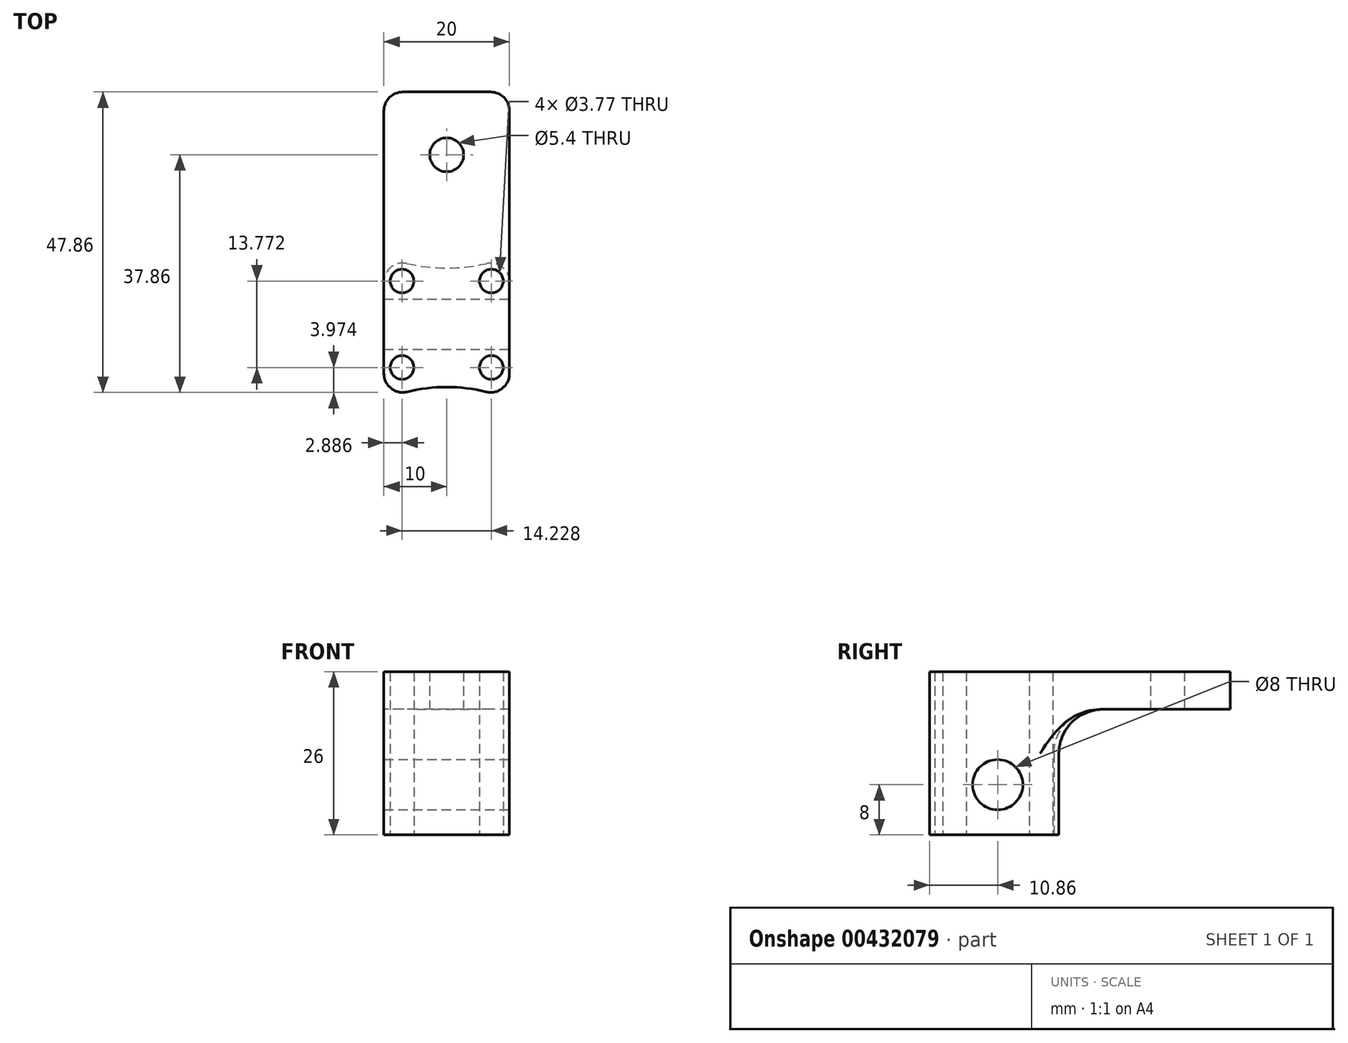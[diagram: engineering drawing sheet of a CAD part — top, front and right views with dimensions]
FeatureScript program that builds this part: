
annotation { "Feature Type Name" : "Feature", "Feature Type Description" : "" }
export const myFeature = defineFeature(function(context is Context, id is Id, definition is map)
    precondition{}
    {
        {
            var Q0;
            Q0=qCreatedBy(makeId("Top.planeOp"),FACE);
            var sketch = newSketch(context, id + "F0", { "sketchPlane" : qUnion([Q0])});
            skLineSegment(sketch, "E0.bottom", {"start": v(10, -24.5) * mm, "end": v(-10, -24.5) * mm});
            skLineSegment(sketch, "E0.top", {"start": v(10, 24.5) * mm, "end": v(-10, 24.5) * mm});
            skLineSegment(sketch, "E0.left", {"start": v(10, -24.5) * mm, "end": v(10, 24.5) * mm});
            skLineSegment(sketch, "E0.right", {"start": v(-10, -24.5) * mm, "end": v(-10, 24.5) * mm});
            skPoint(sketch, "E0.middle", {"position": v(0, 0) * mm});
            skLineSegment(sketch, "E1", {"start": v(-10, 4.5) * mm, "end": v(10, 4.5) * mm, "construction": true});
            skLineSegment(sketch, "E2", {"start": v(-10, -12.5) * mm, "end": v(10, -12.5) * mm, "construction": true});
            skCircle(sketch, "E3", {"center": v(-7.11, -5.61) * mm, "radius": 1.89 * mm});
            skLineSegment(sketch, "E4", {"start": v(-10, -8.5) * mm, "end": v(10, -8.5) * mm, "construction": true});
            skLineSegment(sketch, "E5", {"start": v(-10, -16.5) * mm, "end": v(10, -16.5) * mm, "construction": true});
            skCircle(sketch, "E6.MirrorC", {"center": v(7.11, -5.61) * mm, "radius": 1.89 * mm});
            skCircle(sketch, "E7.MirrorC", {"center": v(7.11, -19.39) * mm, "radius": 1.89 * mm});
            skCircle(sketch, "E8.MirrorC", {"center": v(-7.11, -19.39) * mm, "radius": 1.89 * mm});
            skCircle(sketch, "E9", {"center": v(0, 14.5) * mm, "radius": 2.7 * mm});
            skPoint(sketch, "E9.centerSnap0", {"position": v(0, 24.5) * mm});
            skLineSegment(sketch, "E10", {"start": v(10, -0.5) * mm, "end": v(-10, -0.5) * mm, "construction": true});
            skLineSegment(sketch, "E11", {"start": v(-10, -1.73) * mm, "end": v(10, -1.73) * mm});
            skSolve(sketch);
        }
        {
            var Q0;
            Q0=makeQuery(id+"F0.imprint","IMPRINT",FACE,{"disambiguationData":[TD([[makeQuery(id+"F0.imprint","IMPRINT",EDGE,{"derivedFrom":sQuery(id+"F0.wireOp",EDGE,"E0.bottom")}),-1.0]])]});
            var Q1;
            {var subQ1=sQuery(id+"F0.wireOp",EDGE,"E0.top");Q1=makeQuery(id+"F0.imprint","IMPRINT",FACE,{"disambiguationData":[TD([[makeQuery(id+"F0.imprint","IMPRINT",EDGE,{"derivedFrom":subQ1}),1.0]])]});}
            extrude(context, id + "F1", {"entities" : qUnion([Q0, Q1]), "depth" : 6 * mm});
        }
        {
            var Q0;
            {var subQ1=sQuery(id+"F0.wireOp",EDGE,"E0.bottom");Q0=makeQuery(id+"F0.imprint","IMPRINT",FACE,{"disambiguationData":[TD([[makeQuery(id+"F0.imprint","IMPRINT",EDGE,{"derivedFrom":subQ1}),-1.0]])]});}
            extrude(context, id + "F2", {"entities" : qUnion([Q0]), "operationType" : NewBodyOperationType.ADD, "oppositeDirection" : true, "depth" : 20 * mm});
        }
        {
            var Q0;
            {var subQ0=sQuery(id+"F0.wireOp",EDGE,"E0.left");Q0=makeQuery(id+"F2.boolean.opBoolean","MERGE",FACE,{"derivedFrom":[makeQuery(id+"F1.opExtrude","SWEPT_FACE",FACE,{"disambiguationData":[OSD([subQ0])]}),makeQuery(id+"F2.opExtrude","SWEPT_FACE",FACE,{"disambiguationData":[OSD([subQ0])]})]});}
            var sketch = newSketch(context, id + "F3", { "sketchPlane" : qUnion([Q0])});
            skCircle(sketch, "E12", {"center": v(-12.5, -12) * mm, "radius": 4 * mm});
            skLineSegment(sketch, "E13", {"start": v(-1.73, -12) * mm, "end": v(-24.5, -12) * mm, "construction": true});
            skSolve(sketch);
        }
        {
            var Q0;
            Q0=makeQuery(id+"F3.imprint","IMPRINT",FACE,{"disambiguationData":[TD([[makeQuery(id+"F3.imprint","IMPRINT",EDGE,{"derivedFrom":sQuery(id+"F3.wireOp",EDGE,"E12")}),1.0]])]});
            extrude(context, id + "F4", {"entities" : qUnion([Q0]), "operationType" : NewBodyOperationType.REMOVE, "oppositeDirection" : true, "depth" : 25 * mm});
        }
        {
            var Q0;
            Q0=makeQuery(id+"F2.opExtrude","CAP_FACE",FACE,{"disambiguationData":[OSD([sQuery(id+"F0.wireOp",EDGE,"E0.bottom"),sQuery(id+"F0.wireOp",EDGE,"E0.left"),sQuery(id+"F0.wireOp",EDGE,"E0.right"),sQuery(id+"F0.wireOp",EDGE,"E3"),sQuery(id+"F0.wireOp",EDGE,"E6.MirrorC"),sQuery(id+"F0.wireOp",EDGE,"E7.MirrorC"),sQuery(id+"F0.wireOp",EDGE,"E8.MirrorC"),sQuery(id+"F0.wireOp",EDGE,"E11")])],"isStart":false});
            var sketch = newSketch(context, id + "F5", { "sketchPlane" : qUnion([Q0])});
            skArc(sketch, "E14", {"start": v(10, 1.73) * mm, "mid": v(0, 3.55) * mm, "end": v(-10, 1.73) * mm});
            skArc(sketch, "E15", {"start": v(-10, 24.5) * mm, "mid": v(0, 22.5) * mm, "end": v(10, 24.5) * mm});
            skSolve(sketch);
        }
        {
            var Q0;
            Q0=makeQuery(id+"F5.imprint","IMPRINT",FACE,{"disambiguationData":[TD([[makeQuery(id+"F5.imprint","IMPRINT",EDGE,{"derivedFrom":sQuery(id+"F5.wireOp",EDGE,"E14")}),1.0]])]});
            var Q1;
            Q1=makeQuery(id+"F1.opExtrude","CAP_FACE",FACE,{"disambiguationData":[OSD([sQuery(id+"F0.wireOp",EDGE,"E0.bottom"),sQuery(id+"F0.wireOp",EDGE,"E0.top"),sQuery(id+"F0.wireOp",EDGE,"E0.left"),sQuery(id+"F0.wireOp",EDGE,"E0.right"),sQuery(id+"F0.wireOp",EDGE,"E3"),sQuery(id+"F0.wireOp",EDGE,"E6.MirrorC"),sQuery(id+"F0.wireOp",EDGE,"E7.MirrorC"),sQuery(id+"F0.wireOp",EDGE,"E8.MirrorC"),sQuery(id+"F0.wireOp",EDGE,"E9")])],"isStart":true});
            extrude(context, id + "F6", {"entities" : qUnion([Q0]), "operationType" : NewBodyOperationType.REMOVE, "endBound" : BoundingType.UP_TO_SURFACE, "oppositeDirection" : true, "endBoundEntityFace" : qUnion([Q1]), "depth" : 25 * mm});
        }
        {
            var Q0;
            Q0=makeQuery(id+"F5.imprint","IMPRINT",FACE,{"disambiguationData":[TD([[makeQuery(id+"F5.imprint","IMPRINT",EDGE,{"derivedFrom":sQuery(id+"F5.wireOp",EDGE,"E15")}),1.0]])]});
            extrude(context, id + "F7", {"entities" : qUnion([Q0]), "operationType" : NewBodyOperationType.REMOVE, "endBound" : BoundingType.THROUGH_ALL, "oppositeDirection" : true, "depth" : 25 * mm});
        }
        {
            var Q0;
            Q0=makeQuery(id+"F1.opExtrude","SWEPT_EDGE",EDGE,{"disambiguationData":[OSD([sQuery(id+"F0.wireOp",EDGE,"E0.top"),sQuery(id+"F0.wireOp",EDGE,"E0.right")])]});
            var Q1;
            Q1=makeQuery(id+"F1.opExtrude","SWEPT_EDGE",EDGE,{"disambiguationData":[OSD([sQuery(id+"F0.wireOp",EDGE,"E0.top"),sQuery(id+"F0.wireOp",EDGE,"E0.left")])]});
            var Q2;
            {var subQ0=sQuery(id+"F0.wireOp",EDGE,"E0.left");var subQ1=sQuery(id+"F0.wireOp",EDGE,"E0.bottom");Q2=makeQuery(id+"F7.boolean.opBoolean","MERGE",EDGE,{"derivedFrom":[makeQuery(id+"F2.boolean.opBoolean","MERGE",EDGE,{"derivedFrom":[makeQuery(id+"F1.opExtrude","SWEPT_EDGE",EDGE,{"disambiguationData":[OSD([subQ1,subQ0])]}),makeQuery(id+"F2.opExtrude","SWEPT_EDGE",EDGE,{"disambiguationData":[OSD([subQ1,subQ0])]})]}),makeQuery(id+"F7.opExtrude","SWEPT_EDGE",EDGE,{"disambiguationData":[OSD([subQ1,subQ0,sQuery(id+"F5.wireOp",EDGE,"E15")])]})]});}
            var Q3;
            {var subQ0=sQuery(id+"F0.wireOp",EDGE,"E0.right");var subQ1=sQuery(id+"F0.wireOp",EDGE,"E0.bottom");Q3=makeQuery(id+"F7.boolean.opBoolean","MERGE",EDGE,{"derivedFrom":[makeQuery(id+"F2.boolean.opBoolean","MERGE",EDGE,{"derivedFrom":[makeQuery(id+"F1.opExtrude","SWEPT_EDGE",EDGE,{"disambiguationData":[OSD([subQ1,subQ0])]}),makeQuery(id+"F2.opExtrude","SWEPT_EDGE",EDGE,{"disambiguationData":[OSD([subQ1,subQ0])]})]}),makeQuery(id+"F7.opExtrude","SWEPT_EDGE",EDGE,{"disambiguationData":[OSD([subQ1,subQ0,sQuery(id+"F5.wireOp",EDGE,"E15")])]})]});}
            var Q4;
            {var subQ0=sQuery(id+"F0.wireOp",EDGE,"E11");var subQ1=sQuery(id+"F0.wireOp",EDGE,"E0.right");Q4=makeQuery(id+"F6.boolean.opBoolean","MERGE",EDGE,{"derivedFrom":[makeQuery(id+"F2.opExtrude","SWEPT_EDGE",EDGE,{"disambiguationData":[OSD([subQ1,subQ0])]})],"fromTools":[makeQuery(id+"F6.opExtrude","SWEPT_EDGE",EDGE,{"disambiguationData":[OSD([subQ1,subQ0,sQuery(id+"F5.wireOp",EDGE,"E14")])]})]});}
            var Q5;
            {var subQ0=sQuery(id+"F0.wireOp",EDGE,"E11");var subQ1=sQuery(id+"F0.wireOp",EDGE,"E0.left");Q5=makeQuery(id+"F6.boolean.opBoolean","MERGE",EDGE,{"derivedFrom":[makeQuery(id+"F2.opExtrude","SWEPT_EDGE",EDGE,{"disambiguationData":[OSD([subQ1,subQ0])]})],"fromTools":[makeQuery(id+"F6.opExtrude","SWEPT_EDGE",EDGE,{"disambiguationData":[OSD([subQ1,subQ0,sQuery(id+"F5.wireOp",EDGE,"E14")])]})]});}
            fillet(context, id + "F8", {"entities" : qUnion([Q0, Q1, Q2, Q3, Q4, Q5]), "radius" : 3 * mm, "tangentPropagation" : true, "allowEdgeOverflow" : false});
        }
        {
            var Q0;
            Q0=makeQuery(id+"F6.boolean.opBoolean","COPY",EDGE,{"derivedFrom":makeQuery(id+"F6.opExtrude","CAP_EDGE",EDGE,{"disambiguationData":[OSD([sQuery(id+"F5.wireOp",EDGE,"E14")])],"isStart":false})});
            fillet(context, id + "F9", {"entities" : qUnion([Q0]), "radius" : 7 * mm, "tangentPropagation" : true, "allowEdgeOverflow" : false});
        }
    });
